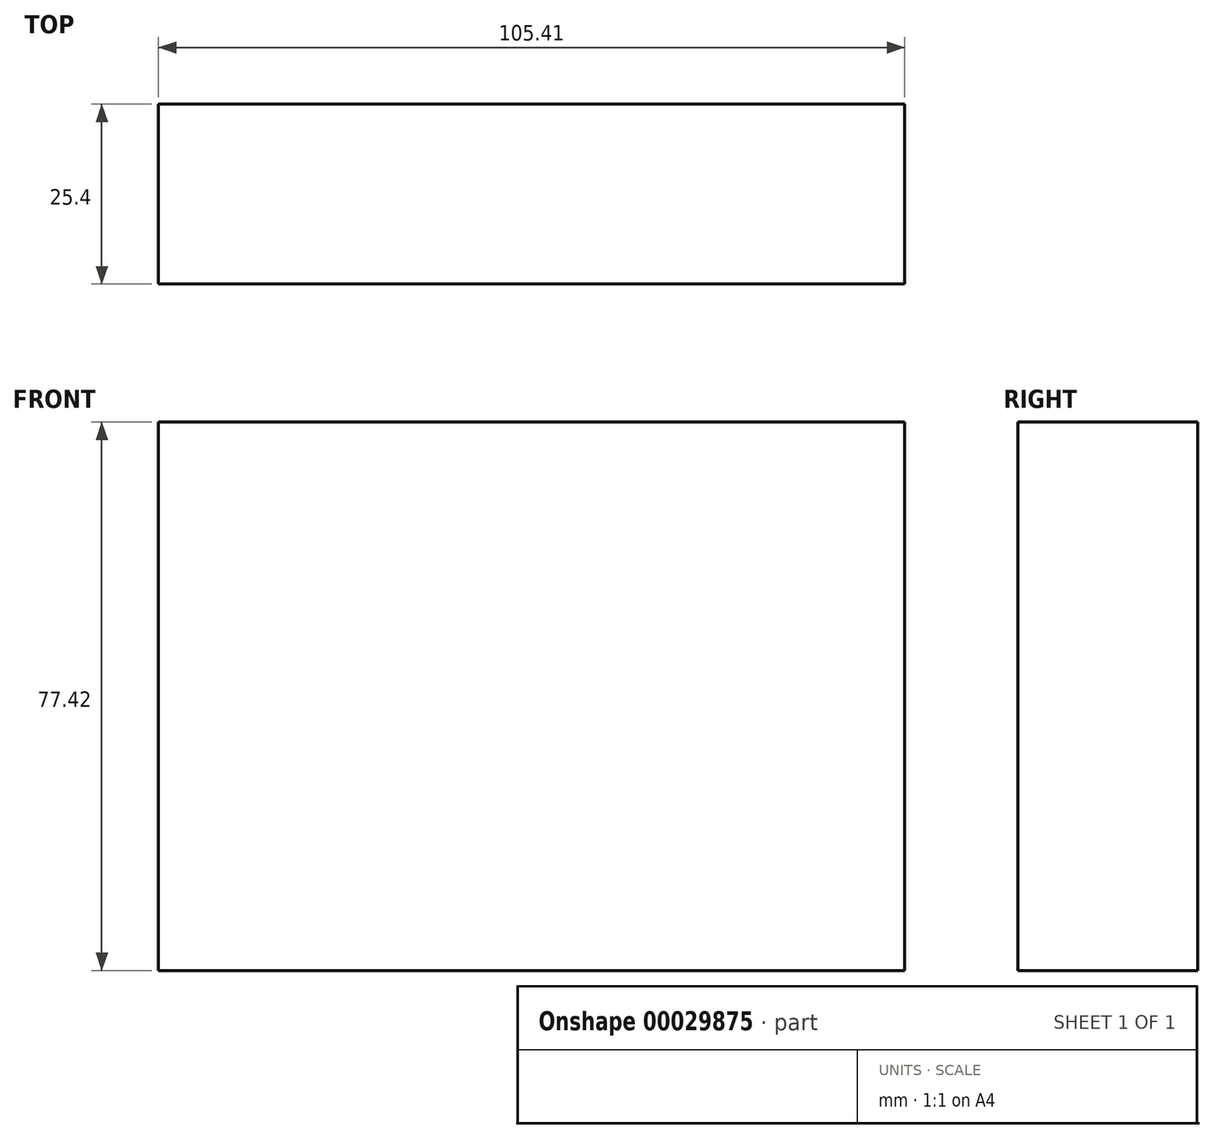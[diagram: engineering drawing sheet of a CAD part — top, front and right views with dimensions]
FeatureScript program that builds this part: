
annotation { "Feature Type Name" : "Feature", "Feature Type Description" : "" }
export const myFeature = defineFeature(function(context is Context, id is Id, definition is map)
    precondition{}
    {
        {
            var Q0;
            Q0=qCreatedBy(makeId("Front.planeOp"),FACE);
            var sketch = newSketch(context, id + "F0", { "sketchPlane" : qUnion([Q0])});
            skLineSegment(sketch, "E0.bottom", {"start": v(-33.65, 62.86) * mm, "end": v(71.76, 62.86) * mm});
            skLineSegment(sketch, "E0.top", {"start": v(-33.65, -14.56) * mm, "end": v(71.76, -14.56) * mm});
            skLineSegment(sketch, "E0.left", {"start": v(-33.65, 62.86) * mm, "end": v(-33.65, -14.56) * mm});
            skLineSegment(sketch, "E0.right", {"start": v(71.76, 62.86) * mm, "end": v(71.76, -14.56) * mm});
            skSolve(sketch);
        }
        {
            var Q0;
            Q0=makeQuery(id+"F0.imprint","IMPRINT",FACE,{"disambiguationData":[TD([[makeQuery(id+"F0.imprint","IMPRINT",EDGE,{"derivedFrom":sQuery(id+"F0.wireOp",EDGE,"E0.bottom")}),-1.0]])]});
            extrude(context, id + "F1", {"entities" : qUnion([Q0]), "depth" : 25.4 * mm});
        }
    });
